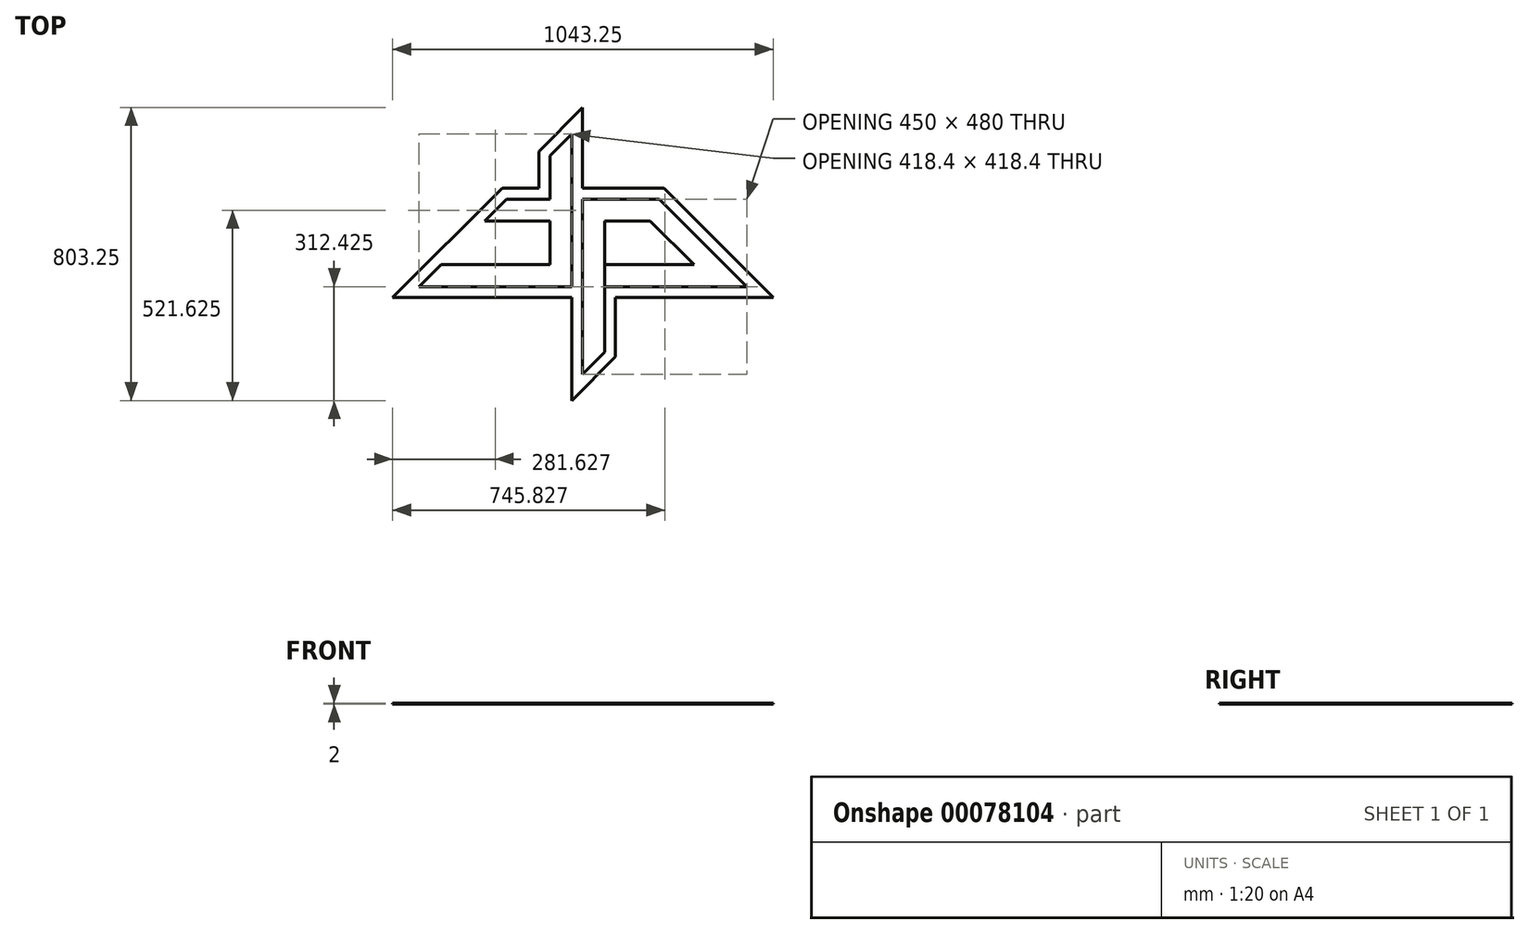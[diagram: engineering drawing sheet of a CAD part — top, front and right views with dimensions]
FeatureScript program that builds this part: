
annotation { "Feature Type Name" : "Feature", "Feature Type Description" : "" }
export const myFeature = defineFeature(function(context is Context, id is Id, definition is map)
    precondition{}
    {
        {
            var Q0;
            Q0=qCreatedBy(makeId("Top.planeOp"),FACE);
            var sketch = newSketch(context, id + "F0", { "sketchPlane" : qUnion([Q0])});
            skLineSegment(sketch, "E0", {"start": v(-409.53, 703.26) * mm, "end": v(-409.53, 189.36) * mm});
            skLineSegment(sketch, "E1", {"start": v(-409.53, -63.07) * mm, "end": v(-439.53, -93.07) * mm});
            skLineSegment(sketch, "E2", {"start": v(-439.53, -93.07) * mm, "end": v(-439.53, 680.18) * mm});
            skLineSegment(sketch, "E3", {"start": v(-499.53, 579.36) * mm, "end": v(-499.53, 459.36) * mm});
            skLineSegment(sketch, "E4", {"start": v(-499.53, 459.36) * mm, "end": v(-660.36, 459.36) * mm});
            skLineSegment(sketch, "E5", {"start": v(-720.36, 399.36) * mm, "end": v(-499.53, 399.36) * mm});
            skLineSegment(sketch, "E6", {"start": v(-499.53, 399.36) * mm, "end": v(-499.53, 279.36) * mm});
            skLineSegment(sketch, "E7", {"start": v(-499.53, 279.36) * mm, "end": v(-840.36, 279.36) * mm});
            skLineSegment(sketch, "E8", {"start": v(-900.36, 219.36) * mm, "end": v(-439.53, 219.36) * mm});
            skLineSegment(sketch, "E9", {"start": v(-966.26, 189.36) * mm, "end": v(-439.53, 189.36) * mm});
            skLineSegment(sketch, "E10", {"start": v(-409.53, 459.36) * mm, "end": v(-157.1, 459.36) * mm});
            skLineSegment(sketch, "E11", {"start": v(-157.1, 459.36) * mm, "end": v(112.9, 189.36) * mm});
            skLineSegment(sketch, "E12", {"start": v(112.9, 189.36) * mm, "end": v(-409.53, 189.36) * mm});
            skLineSegment(sketch, "E13", {"start": v(-409.53, 399.36) * mm, "end": v(-139.53, 399.36) * mm});
            skLineSegment(sketch, "E14", {"start": v(-139.53, 399.36) * mm, "end": v(40.47, 219.36) * mm});
            skLineSegment(sketch, "E15", {"start": v(40.47, 219.36) * mm, "end": v(-349.53, 219.36) * mm});
            skLineSegment(sketch, "E16", {"start": v(-349.53, 219.36) * mm, "end": v(-349.53, 399.36) * mm});
            skLineSegment(sketch, "E17", {"start": v(-499.53, 620.18) * mm, "end": v(-499.53, 579.36) * mm});
            skLineSegment(sketch, "E18", {"start": v(-630.36, 489.36) * mm, "end": v(-529.53, 489.36) * mm});
            skLineSegment(sketch, "E19", {"start": v(-529.53, 489.36) * mm, "end": v(-529.53, 590.18) * mm});
            skLineSegment(sketch, "E20", {"start": v(-409.53, 489.36) * mm, "end": v(-187.1, 489.36) * mm});
            skLineSegment(sketch, "E21", {"start": v(-224.39, 399.36) * mm, "end": v(-44.39, 219.36) * mm});
            skLineSegment(sketch, "E22", {"start": v(-139.53, 399.36) * mm, "end": v(-199.53, 459.36) * mm});
            skLineSegment(sketch, "E23", {"start": v(-104.39, 279.36) * mm, "end": v(-409.53, 279.36) * mm});
            skLineSegment(sketch, "E24", {"start": v(-349.53, 219.36) * mm, "end": v(-349.53, -3.07) * mm});
            skLineSegment(sketch, "E25", {"start": v(-349.53, -3.07) * mm, "end": v(-409.53, -63.07) * mm});
            skLineSegment(sketch, "E26", {"start": v(-349.53, -3.07) * mm, "end": v(-319.53, 26.93) * mm});
            skLineSegment(sketch, "E27", {"start": v(-319.53, 26.93) * mm, "end": v(-319.53, 189.36) * mm});
            skLineSegment(sketch, "E28", {"start": v(-409.53, -20.64) * mm, "end": v(-349.53, 39.36) * mm});
            skLineSegment(sketch, "E29", {"start": v(-349.53, 279.36) * mm, "end": v(-349.53, 219.36) * mm});
            skPoint(sketch, "E30", {"position": v(-889.53, 219.36) * mm});
            skLineSegment(sketch, "E31", {"start": v(-409.53, 189.36) * mm, "end": v(-409.53, -63.07) * mm});
            skLineSegment(sketch, "E32", {"start": v(-157.1, 459.36) * mm, "end": v(-187.1, 489.36) * mm});
            skLineSegment(sketch, "E33", {"start": v(-930.36, 189.36) * mm, "end": v(-409.53, 710.18) * mm});
            skLineSegment(sketch, "E34", {"start": v(-409.53, 703.26) * mm, "end": v(-409.53, 710.18) * mm});
            skLineSegment(sketch, "E35", {"start": v(-887.93, 189.36) * mm, "end": v(-409.53, 667.76) * mm});
            skSolve(sketch);
        }
        {
            var Q0;
            {var subQ0=sQuery(id+"F0.wireOp",EDGE,"E16");var subQ1=sQuery(id+"F0.wireOp",EDGE,"E13");var subQ2=makeQuery(id+"F0.imprint","INTERSECT",VERTEX,{"derivedFrom":[subQ1,subQ0]});Q0=makeQuery(id+"F0.imprint","IMPRINT",FACE,{"disambiguationData":[TD([[makeQuery(id+"F0.imprint","IMPRINT",EDGE,{"disambiguationData":[TD([[subQ2,-1.0]])],"derivedFrom":subQ1}),-1.0]])]});}
            var Q1;
            {var subQ0=sQuery(id+"F0.wireOp",EDGE,"kCgC62i4-3ZIu-GHeE-MCTe-qUS0iTkWxqUm");var subQ1=sQuery(id+"F0.wireOp",EDGE,"E8");var subQ2=makeQuery(id+"F0.imprint","INTERSECT",VERTEX,{"derivedFrom":[subQ1,subQ0]});Q1=makeQuery(id+"F0.imprint","IMPRINT",FACE,{"disambiguationData":[TD([[makeQuery(id+"F0.imprint","IMPRINT",EDGE,{"disambiguationData":[TD([[subQ2,-1.0]])],"derivedFrom":subQ1}),-1.0]])]});}
            var Q2;
            {var subQ0=sQuery(id+"F0.wireOp",EDGE,"E8");var subQ1=sQuery(id+"F0.wireOp",EDGE,"E2");var subQ2=makeQuery(id+"F0.imprint","INTERSECT",VERTEX,{"derivedFrom":[subQ1,subQ0]});Q2=makeQuery(id+"F0.imprint","IMPRINT",FACE,{"disambiguationData":[TD([[makeQuery(id+"F0.imprint","IMPRINT",EDGE,{"disambiguationData":[TD([[subQ2,1.0]])],"derivedFrom":subQ1}),1.0]])]});}
            var Q3;
            {var subQ0=sQuery(id+"F0.wireOp",EDGE,"kCgC62i4-3ZIu-GHeE-MCTe-qUS0iTkWxqUm");var subQ1=sQuery(id+"F0.wireOp",EDGE,"E4");var subQ2=makeQuery(id+"F0.imprint","INTERSECT",VERTEX,{"derivedFrom":[subQ1,subQ0]});Q3=makeQuery(id+"F0.imprint","IMPRINT",FACE,{"disambiguationData":[TD([[makeQuery(id+"F0.imprint","IMPRINT",EDGE,{"disambiguationData":[TD([[subQ2,1.0]])],"derivedFrom":subQ1}),1.0]])]});}
            var Q4;
            {var subQ0=sQuery(id+"F0.wireOp",EDGE,"kCgC62i4-3ZIu-GHeE-MCTe-qUS0iTkWxqUm");var subQ1=sQuery(id+"F0.wireOp",EDGE,"E5");var subQ2=makeQuery(id+"F0.imprint","INTERSECT",VERTEX,{"derivedFrom":[subQ1,subQ0]});Q4=makeQuery(id+"F0.imprint","IMPRINT",FACE,{"disambiguationData":[TD([[makeQuery(id+"F0.imprint","IMPRINT",EDGE,{"disambiguationData":[TD([[subQ2,-1.0]])],"derivedFrom":subQ1}),-1.0]])]});}
            var Q5;
            {var subQ0=sQuery(id+"F0.wireOp",EDGE,"kCgC62i4-3ZIu-GHeE-MCTe-qUS0iTkWxqUm");var subQ1=sQuery(id+"F0.wireOp",EDGE,"E7");var subQ2=makeQuery(id+"F0.imprint","INTERSECT",VERTEX,{"derivedFrom":[subQ1,subQ0]});Q5=makeQuery(id+"F0.imprint","IMPRINT",FACE,{"disambiguationData":[TD([[makeQuery(id+"F0.imprint","IMPRINT",EDGE,{"disambiguationData":[TD([[subQ2,1.0]])],"derivedFrom":subQ1}),1.0]])]});}
            var Q6;
            {var subQ1=sQuery(id+"F0.wireOp",EDGE,"E1");Q6=makeQuery(id+"F0.imprint","IMPRINT",FACE,{"disambiguationData":[TD([[makeQuery(id+"F0.imprint","IMPRINT",EDGE,{"derivedFrom":subQ1}),-1.0]])]});}
            var Q7;
            {var subQ0=sQuery(id+"F0.wireOp",EDGE,"7QDAVpQ1-5lo7-dagO-89cU-M5nfFCcxTim5");Q7=makeQuery(id+"F0.imprint","IMPRINT",FACE,{"disambiguationData":[TD([[makeQuery(id+"F0.imprint","IMPRINT",EDGE,{"derivedFrom":subQ0}),1.0]])]});}
            var Q8;
            {var subQ0=sQuery(id+"F0.wireOp",EDGE,"E6");Q8=makeQuery(id+"F0.imprint","IMPRINT",FACE,{"disambiguationData":[TD([[makeQuery(id+"F0.imprint","IMPRINT",EDGE,{"derivedFrom":subQ0}),-1.0]])]});}
            var Q9;
            {var subQ0=sQuery(id+"F0.wireOp",EDGE,"kCgC62i4-3ZIu-GHeE-MCTe-qUS0iTkWxqUm");var subQ1=sQuery(id+"F0.wireOp",EDGE,"E4");var subQ2=makeQuery(id+"F0.imprint","INTERSECT",VERTEX,{"derivedFrom":[subQ1,subQ0]});Q9=makeQuery(id+"F0.imprint","IMPRINT",FACE,{"disambiguationData":[TD([[makeQuery(id+"F0.imprint","IMPRINT",EDGE,{"disambiguationData":[TD([[subQ2,1.0]])],"derivedFrom":subQ1}),-1.0]])]});}
            var Q10;
            {var subQ5=sQuery(id+"F0.wireOp",EDGE,"E3");Q10=makeQuery(id+"F0.imprint","IMPRINT",FACE,{"disambiguationData":[TD([[makeQuery(id+"F0.imprint","IMPRINT",EDGE,{"derivedFrom":subQ5}),-1.0]])]});}
            var Q11;
            {var subQ0=sQuery(id+"F0.wireOp",EDGE,"E17");Q11=makeQuery(id+"F0.imprint","IMPRINT",FACE,{"disambiguationData":[TD([[makeQuery(id+"F0.imprint","IMPRINT",EDGE,{"derivedFrom":subQ0}),-1.0]])]});}
            var Q12;
            {var subQ3=sQuery(id+"F0.wireOp",EDGE,"E20");Q12=makeQuery(id+"F0.imprint","IMPRINT",FACE,{"disambiguationData":[TD([[makeQuery(id+"F0.imprint","IMPRINT",EDGE,{"derivedFrom":subQ3}),-1.0]])]});}
            var Q13;
            {var subQ1=sQuery(id+"F0.wireOp",EDGE,"E11");Q13=makeQuery(id+"F0.imprint","IMPRINT",FACE,{"disambiguationData":[TD([[makeQuery(id+"F0.imprint","IMPRINT",EDGE,{"derivedFrom":subQ1}),-1.0]])]});}
            var Q14;
            {var subQ4=sQuery(id+"F0.wireOp",EDGE,"E26");Q14=makeQuery(id+"F0.imprint","IMPRINT",FACE,{"disambiguationData":[TD([[makeQuery(id+"F0.imprint","IMPRINT",EDGE,{"derivedFrom":subQ4}),1.0]])]});}
            var Q15;
            {var subQ0=sQuery(id+"F0.wireOp",EDGE,"E25");Q15=makeQuery(id+"F0.imprint","IMPRINT",FACE,{"disambiguationData":[TD([[makeQuery(id+"F0.imprint","IMPRINT",EDGE,{"derivedFrom":subQ0}),-1.0]])]});}
            var Q16;
            {var subQ3=sQuery(id+"F0.wireOp",EDGE,"E29");Q16=makeQuery(id+"F0.imprint","IMPRINT",FACE,{"disambiguationData":[TD([[makeQuery(id+"F0.imprint","IMPRINT",EDGE,{"derivedFrom":subQ3}),-1.0]])]});}
            var Q17;
            {var subQ3=sQuery(id+"F0.wireOp",EDGE,"E17");Q17=makeQuery(id+"F0.imprint","IMPRINT",FACE,{"disambiguationData":[TD([[makeQuery(id+"F0.imprint","IMPRINT",EDGE,{"derivedFrom":subQ3}),1.0]])]});}
            var Q18;
            {var subQ5=sQuery(id+"F0.wireOp",EDGE,"E34");Q18=makeQuery(id+"F0.imprint","IMPRINT",FACE,{"disambiguationData":[TD([[makeQuery(id+"F0.imprint","IMPRINT",EDGE,{"derivedFrom":subQ5}),1.0]])]});}
            var Q19;
            {var subQ6=sQuery(id+"F0.wireOp",EDGE,"E4");var subQ7=sQuery(id+"F0.wireOp",EDGE,"E3");var subQ8=makeQuery(id+"F0.imprint","INTERSECT",VERTEX,{"derivedFrom":[subQ7,subQ6]});Q19=makeQuery(id+"F0.imprint","IMPRINT",FACE,{"disambiguationData":[TD([[makeQuery(id+"F0.imprint","IMPRINT",EDGE,{"disambiguationData":[TD([[subQ8,1.0]])],"derivedFrom":subQ7}),-1.0]])]});}
            extrude(context, id + "F1", {"entities" : qUnion([Q0, Q1, Q2, Q3, Q4, Q5, Q6, Q7, Q8, Q9, Q10, Q11, Q12, Q13, Q14, Q15, Q16, Q17, Q18, Q19]), "depth" : 2 * mm});
        }
    });
